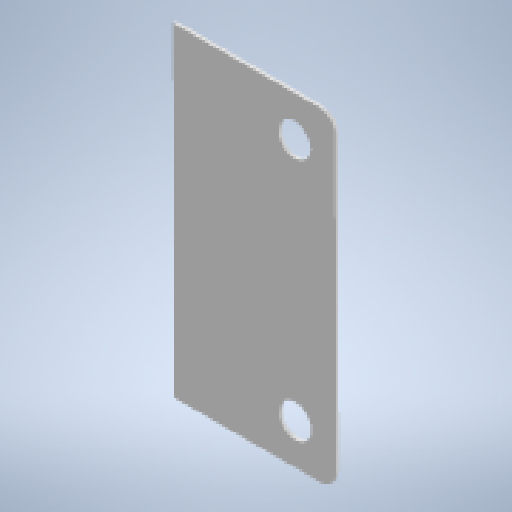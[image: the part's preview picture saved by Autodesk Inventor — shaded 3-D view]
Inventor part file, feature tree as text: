
AUTODESK INVENTOR PART (.ipt)
format: ipt  version: 2025 (Build 290162000, 162)  size: 137,216 bytes
history: native  units: mm
features: reference x7, extrude x1, sketch x1, other x1
ambient origin geometry x8: Origin, YZ Plane, XZ Plane, XY Plane, X Axis, Y Axis, Z Axis, Center Point
bodies: Solid1 (feature_tree)
feature tree (10):
  extrude  "Extrusion1"  Depth=0.2mm TaperAngle=0.0deg
  sketch  "Sketch1"  dims[d0=10.0mm d1=0.2mm d2=0.0mm]
  reference  "Reference1"
  reference  "Reference2"
  reference  "Reference3"
  reference  "Reference4"
  reference  "Reference5"
  reference  "Reference6"
  reference  "Reference7"
  other  "tamale_flex.iam"
